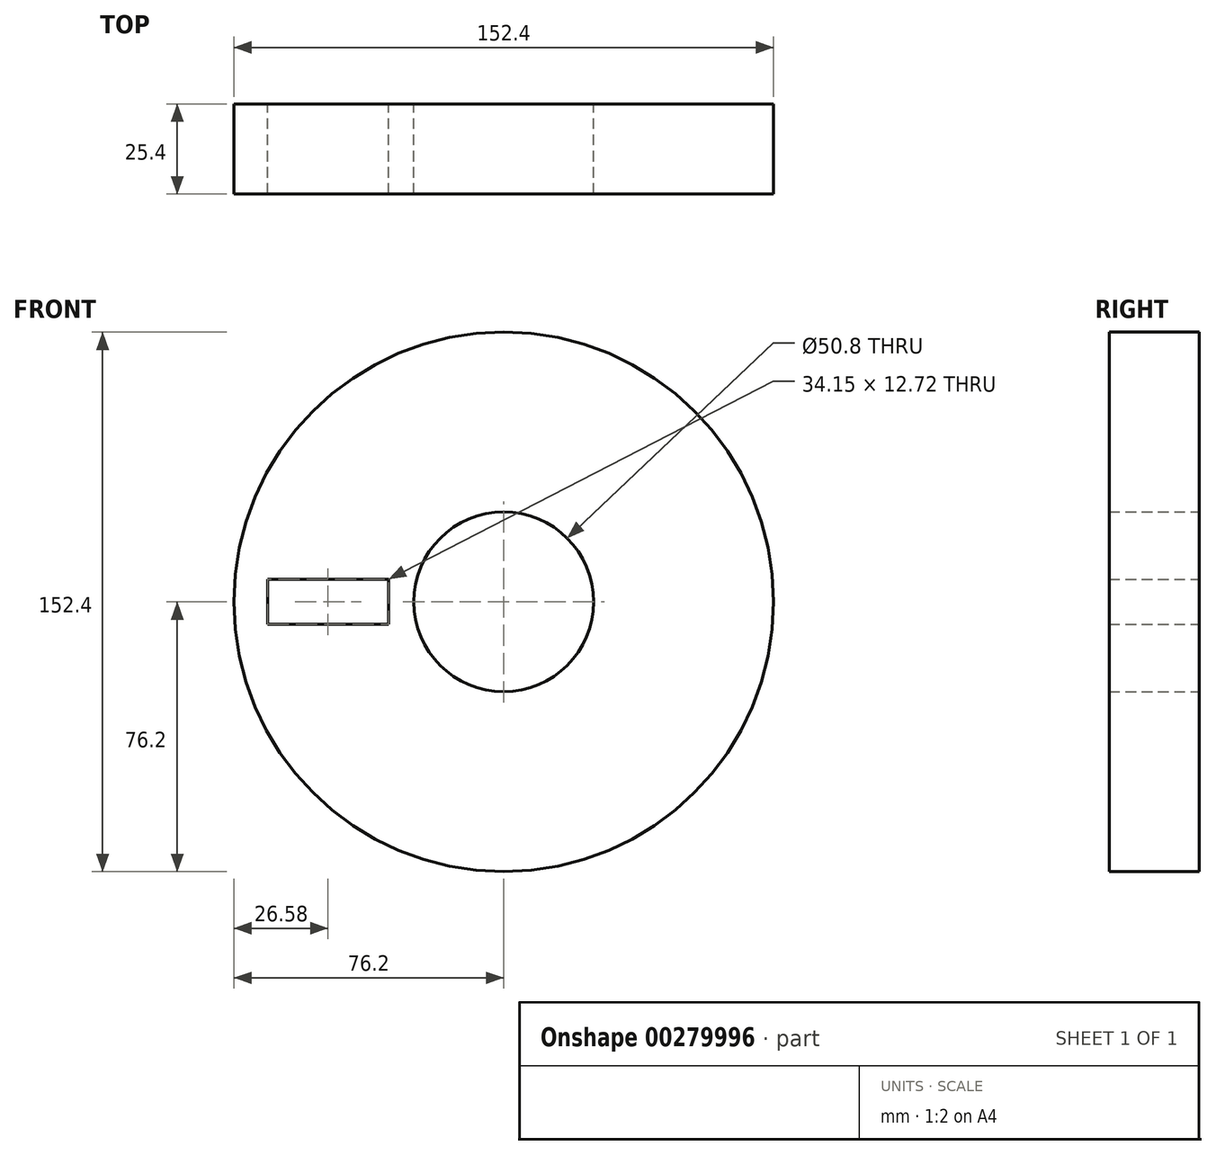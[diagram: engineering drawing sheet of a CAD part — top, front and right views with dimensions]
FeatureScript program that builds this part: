
annotation { "Feature Type Name" : "Feature", "Feature Type Description" : "" }
export const myFeature = defineFeature(function(context is Context, id is Id, definition is map)
    precondition{}
    {
        {
            var Q0;
            Q0=qCreatedBy(makeId("Front.planeOp"),FACE);
            var sketch = newSketch(context, id + "F0", { "sketchPlane" : qUnion([Q0])});
            skCircle(sketch, "E0", {"center": v(0, 0) * mm, "radius": 76.2 * mm});
            skCircle(sketch, "E1", {"center": v(0, 0) * mm, "radius": 25.4 * mm});
            skLineSegment(sketch, "E2.bottom", {"start": v(-32.54, 6.36) * mm, "end": v(-66.7, 6.36) * mm});
            skLineSegment(sketch, "E2.top", {"start": v(-32.54, -6.36) * mm, "end": v(-66.7, -6.36) * mm});
            skLineSegment(sketch, "E2.left", {"start": v(-32.54, 6.36) * mm, "end": v(-32.54, -6.36) * mm});
            skLineSegment(sketch, "E2.right", {"start": v(-66.7, 6.36) * mm, "end": v(-66.7, -6.36) * mm});
            skPoint(sketch, "E2.middle", {"position": v(-49.62, 0) * mm});
            skSolve(sketch);
        }
        {
            var Q0;
            Q0 = qSketchRegion(id + "F0", true);
            var Q1;
            Q1=makeQuery(id+"F0.imprint","IMPRINT",FACE,{"disambiguationData":[TD([[makeQuery(id+"F0.imprint","IMPRINT",EDGE,{"derivedFrom":sQuery(id+"F0.wireOp",EDGE,"E0")}),1.0]])]});
            extrude(context, id + "F1", {"entities" : qUnion([Q0, Q1]), "depth" : 25.4 * mm});
        }
    });
